# Revit family: HC_Storage Tank_MEPcontent_De Dietrich Thermique_RSB
name_source: partatom
category: Mechanical Equipment
revit_build: Autodesk Revit 2018 (Build: 20170223_1515(x64)
units: mm (PartAtom-declared; Revit-internal decimal feet)

## family parameters
Always vertical = Yes
Cut with Voids When Loaded = No
OmniClass Number = 23.75.10.34.11
OmniClass Title = Energy Storage Tanks
Part Type = Normal
Room Calculation Point = No
Round Connector Dimension = Use Diameter
Shared = No
Work Plane-Based = No

## types (6) — shared parameters
Article Description = Storage tank
Black = Color RGB 045-045-045
Boiler Sensor Position = 22.50°
Content Supplier URL = www.MEPcontent.com
Custom = No
Description = Storage tank
Domestic Hot Water Connection Diameter = 51 mm
Drain Diameter = 32 mm  [stored 0.104987 ft]
EMCS Version = 2.0
ETIM Article Class = EC010184
Family Version = 11.14
Grey = Color RAL 9006
Hydronic Return Connection Diameter = 51 mm
Hydronic Supply Connection Diameter = 51 mm
IFCExportAs = IfcTankType
IFCExportType = NOTDEFINED
MEPcontent Class = STORAGE_TANK_HC
Manufacturer = De Dietrich Thermique
Manufacturer URL = http://pro.dedietrich-thermique.fr
Product Line = De Dietrich Thermique
Revit Version = 2018
Secondary Domestic Hot Water Connection Diameter = 38 mm
URL = www.stabiplan.com
Use Nominal Diameter = Yes
White = Color RAL 9016

## per-type parameters (varying)
| type | A | B | Bottom Geometry | C | D | DCW Pos | E | F | GTIN | H | L | Manufacturer Art. No. | Tank Radius | Tank Rail Diameter | Top Geometry | Volume |
| RSB 800 NV | 1000 mm  [stored 3.28084 ft] | 1125 mm | 41 mm | 1255 mm | 1398 mm | 530 mm | 1826 mm | 520 mm  [stored 1.70604 ft] | 3661238510180 | 346 mm  [stored 1.13517 ft] | 1900 mm | 100017469 | 470 mm  [stored 1.54199 ft] | 1005 mm  [stored 3.29724 ft] | 61 mm | 800.0 L |
| RSB 1000 NV | 1050 mm | 1232 mm | 44 mm | 1374 mm | 1530 mm | 555 mm | 2000 mm | 569 mm  [stored 1.8668 ft] | 3661238495937 | 380 mm | 2075 mm | 100017472 | 495 mm  [stored 1.62402 ft] | 1055 mm | 67 mm | 1000.0 L |
| RSB 1500 NV | 1200 mm | 1300 mm | 47 mm | 1450 mm | 1615 mm | 630 mm  [stored 2.06693 ft] | 2110 mm | 600 mm | 3661238495968 | 400 mm  [stored 1.31234 ft] | 2185 mm | 100017475 | 570 mm  [stored 1.87008 ft] | 1206 mm | 70 mm | 1500.0 L |
| RSB 2000 NV | 1400 mm | 1274 mm | 46 mm | 1421 mm | 1583 mm | 730 mm  [stored 2.39501 ft] | 2068 mm | 588 mm  [stored 1.92913 ft] | 3661238495975 | 392 mm  [stored 1.28609 ft] | 2143 mm | 100017476 | 670 mm | 1407 mm | 69 mm | 2000.0 L |
| RSB 2500 NV | 1400 mm | 1584 mm | 57 mm | 1766 mm | 1967 mm | 730 mm  [stored 2.39501 ft] | 2570 mm | 731 mm  [stored 2.39829 ft] | 3661238495982 | 487 mm  [stored 1.59777 ft] | 2645 mm | 100017477 | 670 mm | 1407 mm | 86 mm | 2500.0 L |
| RSB 3000 NV | 1400 mm | 1725 mm | 62 mm | 1924 mm | 2143 mm | 730 mm  [stored 2.39501 ft] | 2800 mm | 796 mm  [stored 2.61155 ft] | 3661238495999 | 531 mm  [stored 1.74213 ft] | 2875 mm | 100017478 | 670 mm | 1407 mm | 93 mm | 3000.0 L |

note: column(s) folded — value = type name in every type: Article Type, Model

note: [stored X ft] marks values corroborated as IEEE doubles in the binary element streams (Revit-internal decimal feet)

## geometry (parser evidence)
native form markers: Sweep x2
no freeform markers — native parametric forms only
